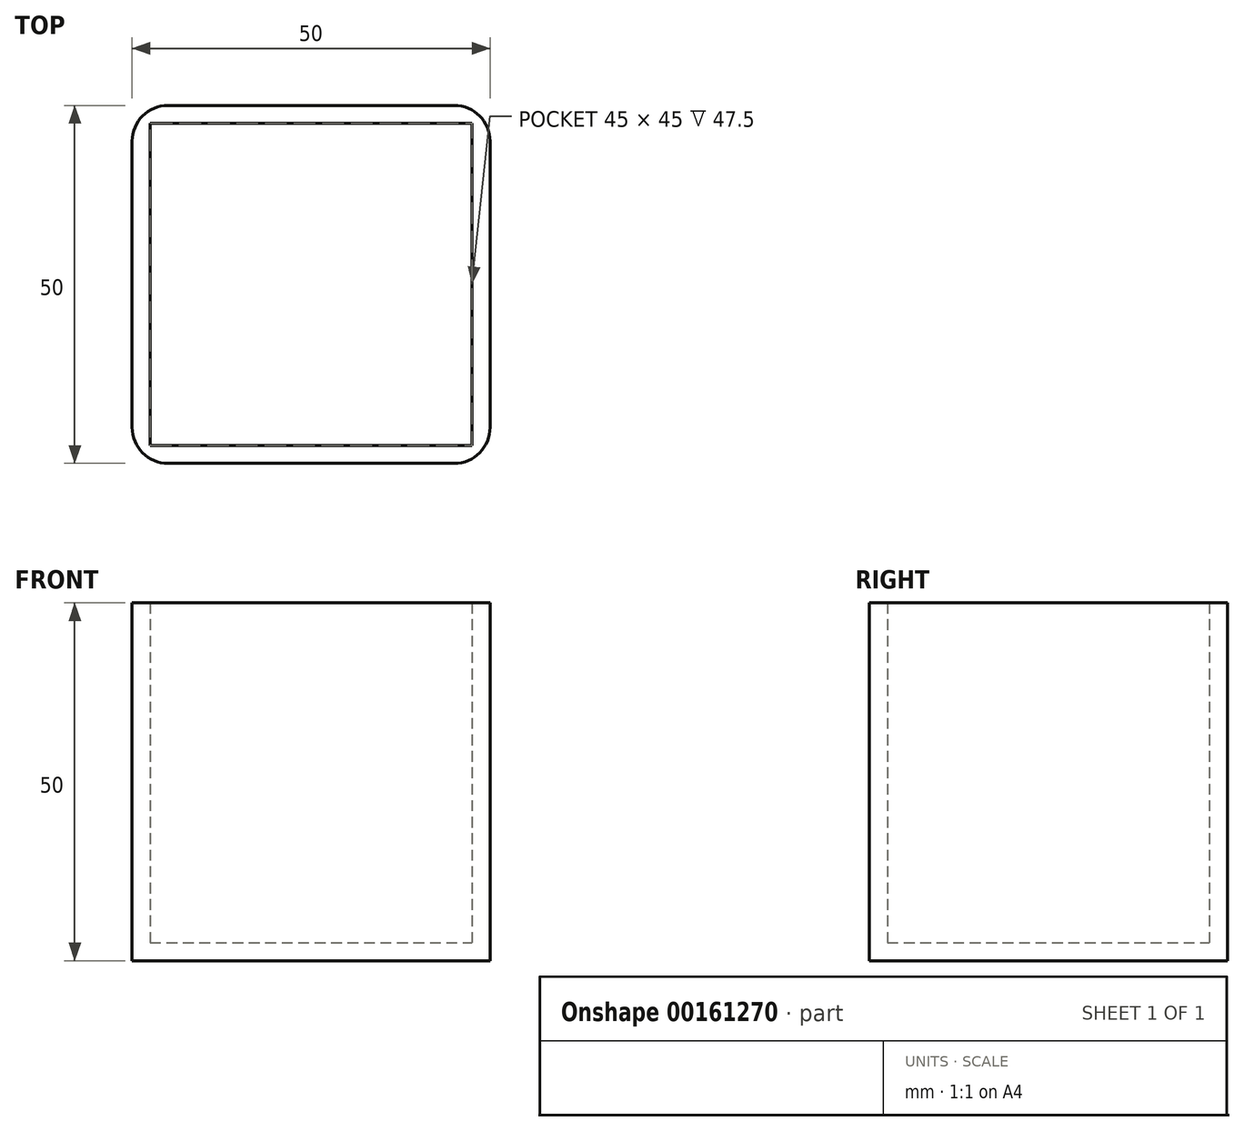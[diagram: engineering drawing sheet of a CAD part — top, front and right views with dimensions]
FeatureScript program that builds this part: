
annotation { "Feature Type Name" : "Feature", "Feature Type Description" : "" }
export const myFeature = defineFeature(function(context is Context, id is Id, definition is map)
    precondition{}
    {
        {
            var Q0;
            Q0=qCreatedBy(makeId("Top.planeOp"),FACE);
            var sketch = newSketch(context, id + "F0", { "sketchPlane" : qUnion([Q0])});
            skLineSegment(sketch, "E0.bottom", {"start": v(-25, -25) * mm, "end": v(25, -25) * mm});
            skLineSegment(sketch, "E0.top", {"start": v(-25, 25) * mm, "end": v(25, 25) * mm});
            skLineSegment(sketch, "E0.left", {"start": v(-25, -25) * mm, "end": v(-25, 25) * mm});
            skLineSegment(sketch, "E0.right", {"start": v(25, -25) * mm, "end": v(25, 25) * mm});
            skPoint(sketch, "E0.middle", {"position": v(0, 0) * mm});
            skSolve(sketch);
        }
        {
            var Q0;
            Q0=makeQuery(id+"F0.imprint","IMPRINT",FACE,{"disambiguationData":[TD([[makeQuery(id+"F0.imprint","IMPRINT",EDGE,{"derivedFrom":sQuery(id+"F0.wireOp",EDGE,"E0.bottom")}),1.0]])]});
            extrude(context, id + "F1", {"entities" : qUnion([Q0]), "depth" : 50 * mm});
        }
        {
            var Q0;
            Q0=makeQuery(id+"F1.opExtrude","CAP_FACE",FACE,{"disambiguationData":[OSD([sQuery(id+"F0.wireOp",EDGE,"E0.bottom"),sQuery(id+"F0.wireOp",EDGE,"E0.top"),sQuery(id+"F0.wireOp",EDGE,"E0.left"),sQuery(id+"F0.wireOp",EDGE,"E0.right")])],"isStart":false});
            shell(context, id + "F2", {"entities" : qUnion([Q0]), "thickness" : 2.5 * mm});
        }
        {
            var Q0;
            Q0=makeQuery(id+"F1.opExtrude","SWEPT_EDGE",EDGE,{"disambiguationData":[OSD([sQuery(id+"F0.wireOp",EDGE,"E0.bottom"),sQuery(id+"F0.wireOp",EDGE,"E0.left")])]});
            var Q1;
            Q1=makeQuery(id+"F1.opExtrude","SWEPT_EDGE",EDGE,{"disambiguationData":[OSD([sQuery(id+"F0.wireOp",EDGE,"E0.bottom"),sQuery(id+"F0.wireOp",EDGE,"E0.right")])]});
            var Q2;
            Q2=makeQuery(id+"F1.opExtrude","SWEPT_EDGE",EDGE,{"disambiguationData":[OSD([sQuery(id+"F0.wireOp",EDGE,"E0.top"),sQuery(id+"F0.wireOp",EDGE,"E0.right")])]});
            var Q3;
            Q3=makeQuery(id+"F1.opExtrude","SWEPT_EDGE",EDGE,{"disambiguationData":[OSD([sQuery(id+"F0.wireOp",EDGE,"E0.top"),sQuery(id+"F0.wireOp",EDGE,"E0.left")])]});
            fillet(context, id + "F3", {"entities" : qUnion([Q0, Q1, Q2, Q3]), "radius" : 5 * mm, "tangentPropagation" : true, "allowEdgeOverflow" : false});
        }
    });
